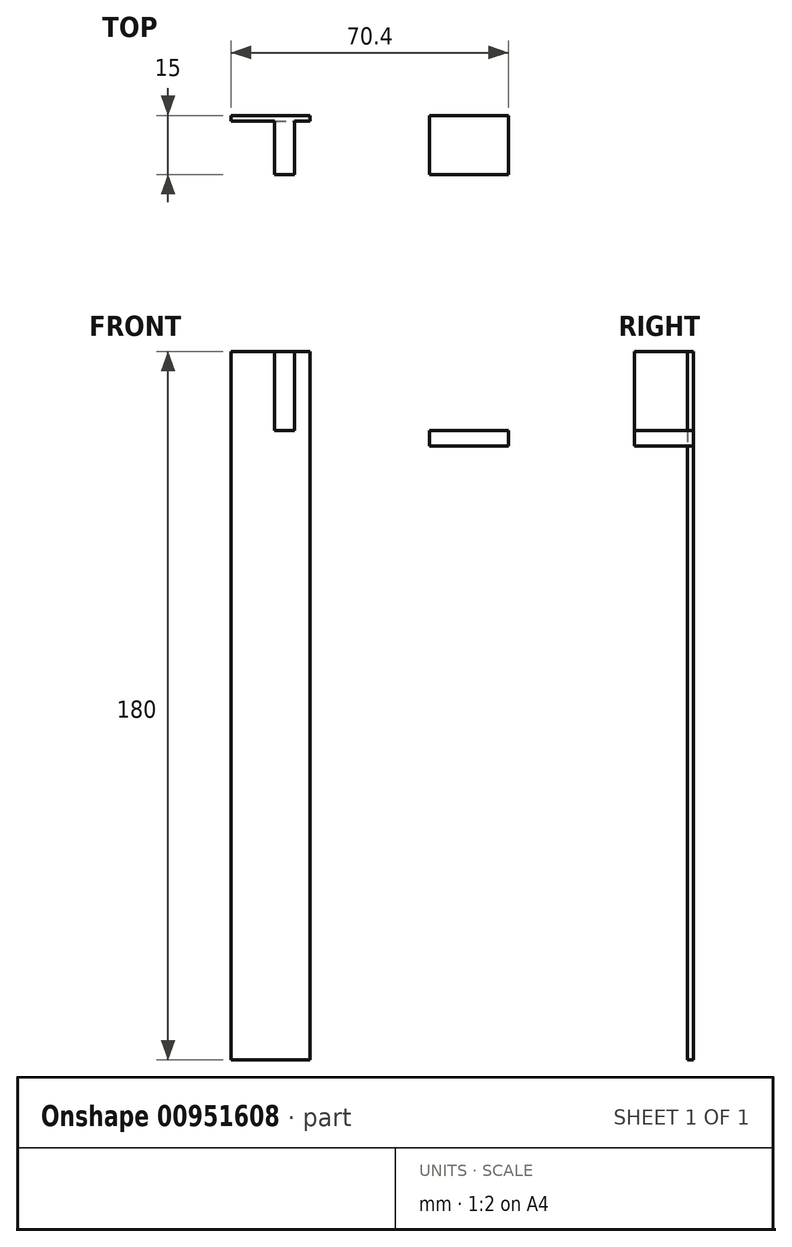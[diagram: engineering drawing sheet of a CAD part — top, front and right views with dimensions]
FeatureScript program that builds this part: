
annotation { "Feature Type Name" : "Feature", "Feature Type Description" : "" }
export const myFeature = defineFeature(function(context is Context, id is Id, definition is map)
    precondition{}
    {
        {
            assignVariable(context, id + "F0", {"name" : "Height", "anyValue" : 18});
        }
        {
            assignVariable(context, id + "F1", {"name" : "Thickness", "anyValue" : 1.5});
        }
        {
            assignVariable(context, id + "F2", {"name" : "Width", "anyValue" : 2});
        }
        {
            assignVariable(context, id + "F3", {"name" : "Gear_Radius", "anyValue" : 1.5});
        }
        {
            assignVariable(context, id + "F4", {"name" : "Wheel_Length", "anyValue" : 2.54});
        }
        {
            assignVariable(context, id + "F5", {"name" : "Second_Jut_Height", "anyValue" : 4});
        }
        {
            var Q0;
            Q0=qCreatedBy(makeId("Front.planeOp"),FACE);
            cPlane(context, id + "F6", {"entities" : qUnion([Q0]), "cplaneType" : CPlaneType.OFFSET, "offset" : 7.5 * mm, "oppositeDirection" : true, "width" : 150 * mm, "height" : 150 * mm});
        }
        {
            var Q0;
            Q0=qCreatedBy(id+"F6.planeOp",FACE);
            var sketch = newSketch(context, id + "F7", { "sketchPlane" : qUnion([Q0])});
            skLineSegment(sketch, "E0.bottom", {"start": v(10, 90) * mm, "end": v(-10, 90) * mm});
            skLineSegment(sketch, "E0.top", {"start": v(10, -90) * mm, "end": v(-10, -90) * mm});
            skLineSegment(sketch, "E0.left", {"start": v(10, 90) * mm, "end": v(10, -90) * mm});
            skLineSegment(sketch, "E0.right", {"start": v(-10, 90) * mm, "end": v(-10, -90) * mm});
            skPoint(sketch, "E1", {"position": v(0, 90) * mm});
            skPoint(sketch, "E2", {"position": v(0, -90) * mm});
            skPoint(sketch, "E3", {"position": v(-10, 0) * mm});
            skPoint(sketch, "E4", {"position": v(10, 0) * mm});
            skSolve(sketch);
        }
        {
            var Q0;
            Q0=qSketchRegion(id+"F7",true);
            extrude(context, id + "F8", {"entities" : qUnion([Q0]), "depth" : (getVariable(context, 'Thickness')) * mm, "offsetDistance" : 25 * mm});
        }
        {
            var Q0;
            Q0=qCreatedBy(makeId("Top.planeOp"),FACE);
            cPlane(context, id + "F9", {"entities" : qUnion([Q0]), "cplaneType" : CPlaneType.OFFSET, "offset" : (getVariable(context, 'Height') / 2) * mm, "oppositeDirection" : true, "width" : 150 * mm, "height" : 150 * mm});
        }
        {
            var Q0;
            Q0=qCreatedBy(id+"F9.planeOp",FACE);
            var sketch = newSketch(context, id + "F10", { "sketchPlane" : qUnion([Q0])});
            skLineSegment(sketch, "E5.bottom", {"start": v(10, 1.55) * mm, "end": v(-10, 1.55) * mm});
            skLineSegment(sketch, "E5.top", {"start": v(10, -1.55) * mm, "end": v(-10, -1.55) * mm});
            skLineSegment(sketch, "E5.left", {"start": v(10, 1.55) * mm, "end": v(10, -1.55) * mm});
            skLineSegment(sketch, "E5.right", {"start": v(-10, 1.55) * mm, "end": v(-10, -1.55) * mm});
            skPoint(sketch, "E5.middle", {"position": v(0, 0) * mm});
            skPoint(sketch, "E6.0", {"position": v(0, -7.5) * mm});
            skPoint(sketch, "E7.0", {"position": v(10, 0) * mm});
            skSolve(sketch);
        }
        {
            var Q0;
            Q0=qSketchRegion(id+"F10",true);
            extrude(context, id + "F11", {"entities" : qUnion([Q0]), "operationType" : NewBodyOperationType.REMOVE, "depth" : (getVariable(context, 'Gear_Radius') / 2) * mm, "offsetDistance" : 25 * mm});
        }
        {
            var Q0;
            Q0=qCreatedBy(makeId("Right.planeOp"),FACE);
            cPlane(context, id + "F12", {"entities" : qUnion([Q0]), "cplaneType" : CPlaneType.OFFSET, "offset" : (getVariable(context, 'Width') / 2) * mm, "width" : 150 * mm, "height" : 150 * mm});
        }
        {
            var Q0;
            Q0=qCreatedBy(id+"F12.planeOp",FACE);
            var sketch = newSketch(context, id + "F13", { "sketchPlane" : qUnion([Q0])});
            skLineSegment(sketch, "E8.bottom", {"start": v(7.5, 90) * mm, "end": v(-7.5, 90) * mm});
            skLineSegment(sketch, "E8.top", {"start": v(7.5, 70) * mm, "end": v(-7.5, 70) * mm});
            skLineSegment(sketch, "E8.left", {"start": v(7.5, 90) * mm, "end": v(7.5, 70) * mm});
            skLineSegment(sketch, "E8.right", {"start": v(-7.5, 90) * mm, "end": v(-7.5, 70) * mm});
            skPoint(sketch, "E8.middle", {"position": v(0, 80) * mm});
            skLineSegment(sketch, "E9.0.0", {"start": v(-1.55, -82.5) * mm, "end": v(1.55, -82.5) * mm, "construction": true});
            skLineSegment(sketch, "E9.0.1", {"start": v(1.55, -82.5) * mm, "end": v(1.55, -90) * mm, "construction": true});
            skLineSegment(sketch, "E9.0.2", {"start": v(1.55, -90) * mm, "end": v(7.5, -90) * mm, "construction": true});
            skLineSegment(sketch, "E9.0.3", {"start": v(7.5, -90) * mm, "end": v(7.5, 90) * mm, "construction": true});
            skLineSegment(sketch, "E9.0.4", {"start": v(7.5, 90) * mm, "end": v(-7.5, 90) * mm, "construction": true});
            skLineSegment(sketch, "E9.0.5", {"start": v(-7.5, 90) * mm, "end": v(-7.5, -90) * mm, "construction": true});
            skLineSegment(sketch, "E9.0.6", {"start": v(-7.5, -90) * mm, "end": v(-1.55, -90) * mm, "construction": true});
            skLineSegment(sketch, "E9.0.7", {"start": v(-1.55, -90) * mm, "end": v(-1.55, -82.5) * mm, "construction": true});
            skPoint(sketch, "E10", {"position": v(7.5, 80) * mm});
            skPoint(sketch, "E11", {"position": v(-7.5, 80) * mm});
            skPoint(sketch, "E12", {"position": v(0, 90) * mm});
            skPoint(sketch, "E13", {"position": v(0, 70) * mm});
            skSolve(sketch);
        }
        {
            var Q0;
            Q0=qSketchRegion(id+"F13",true);
            extrude(context, id + "F14", {"entities" : qUnion([Q0]), "operationType" : NewBodyOperationType.ADD, "depth" : ((getVariable(context, 'Wheel_Length')) + getVariable(context, 'Thickness') + 1) * mm, "offsetDistance" : 25 * mm});
        }
        {
            var Q0;
            Q0=makeQuery(id+"F14.opExtrude","SWEPT_FACE",FACE,{"disambiguationData":[OSD([sQuery(id+"F13.wireOp",EDGE,"E8.top")])]});
            cPlane(context, id + "F15", {"entities" : qUnion([Q0]), "cplaneType" : CPlaneType.OFFSET, "offset" : 0 * mm, "width" : 150 * mm, "height" : 150 * mm});
        }
        {
            var Q0;
            Q0=qCreatedBy(id+"F15.planeOp",FACE);
            var sketch = newSketch(context, id + "F16", { "sketchPlane" : qUnion([Q0])});
            skLineSegment(sketch, "E14.bottom", {"start": v(60.4, 7.5) * mm, "end": v(40.4, 7.5) * mm});
            skLineSegment(sketch, "E14.top", {"start": v(60.4, -7.5) * mm, "end": v(40.4, -7.5) * mm});
            skLineSegment(sketch, "E14.left", {"start": v(60.4, 7.5) * mm, "end": v(60.4, -7.5) * mm});
            skLineSegment(sketch, "E14.right", {"start": v(40.4, 7.5) * mm, "end": v(40.4, -7.5) * mm});
            skPoint(sketch, "E14.middle", {"position": v(50.4, 0) * mm});
            skLineSegment(sketch, "E15.0.0", {"start": v(10, 7.5) * mm, "end": v(10, -7.5) * mm, "construction": true});
            skLineSegment(sketch, "E15.0.1", {"start": v(10, -7.5) * mm, "end": v(60.4, -7.5) * mm, "construction": true});
            skLineSegment(sketch, "E15.0.2", {"start": v(60.4, -7.5) * mm, "end": v(60.4, 7.5) * mm, "construction": true});
            skLineSegment(sketch, "E15.0.3", {"start": v(60.4, 7.5) * mm, "end": v(10, 7.5) * mm, "construction": true});
            skPoint(sketch, "E16", {"position": v(60.4, 0) * mm});
            skPoint(sketch, "E17", {"position": v(40.4, 0) * mm});
            skPoint(sketch, "E18", {"position": v(50.4, -7.5) * mm});
            skPoint(sketch, "E19", {"position": v(50.4, 7.5) * mm});
            skLineSegment(sketch, "E20.0", {"start": v(60.4, 7.5) * mm, "end": v(-10, 7.5) * mm});
            skSolve(sketch);
        }
        {
            var Q0;
            Q0=qSketchRegion(id+"F16",true);
            extrude(context, id + "F17", {"entities" : qUnion([Q0]), "operationType" : NewBodyOperationType.ADD, "depth" : (getVariable(context, 'Second_Jut_Height')) * mm, "offsetDistance" : 25 * mm});
        }
        {
            var Q0;
            Q0=makeQuery(id+"F17.boolean.opBoolean","MERGE",FACE,{"derivedFrom":[makeQuery(id+"F14.opExtrude","CAP_FACE",FACE,{"disambiguationData":[OSD([sQuery(id+"F13.wireOp",EDGE,"E8.bottom"),sQuery(id+"F13.wireOp",EDGE,"E8.top"),sQuery(id+"F13.wireOp",EDGE,"E8.left"),sQuery(id+"F13.wireOp",EDGE,"E8.right")])],"isStart":false}),makeQuery(id+"F17.opExtrude","SWEPT_FACE",FACE,{"disambiguationData":[OSD([sQuery(id+"F16.wireOp",EDGE,"E14.left")])]})]});
            var sketch = newSketch(context, id + "F18", { "sketchPlane" : qUnion([Q0])});
            skCircle(sketch, "E21", {"center": v(0, 50) * mm, "radius": 1.59 * mm});
            skSolve(sketch);
        }
        {
            var Q0;
            Q0=qSketchRegion(id+"F18",true);
            extrude(context, id + "F19", {"entities" : qUnion([Q0]), "operationType" : NewBodyOperationType.REMOVE, "oppositeDirection" : true, "depth" : 100 * mm, "offsetDistance" : 25 * mm});
        }
    });
